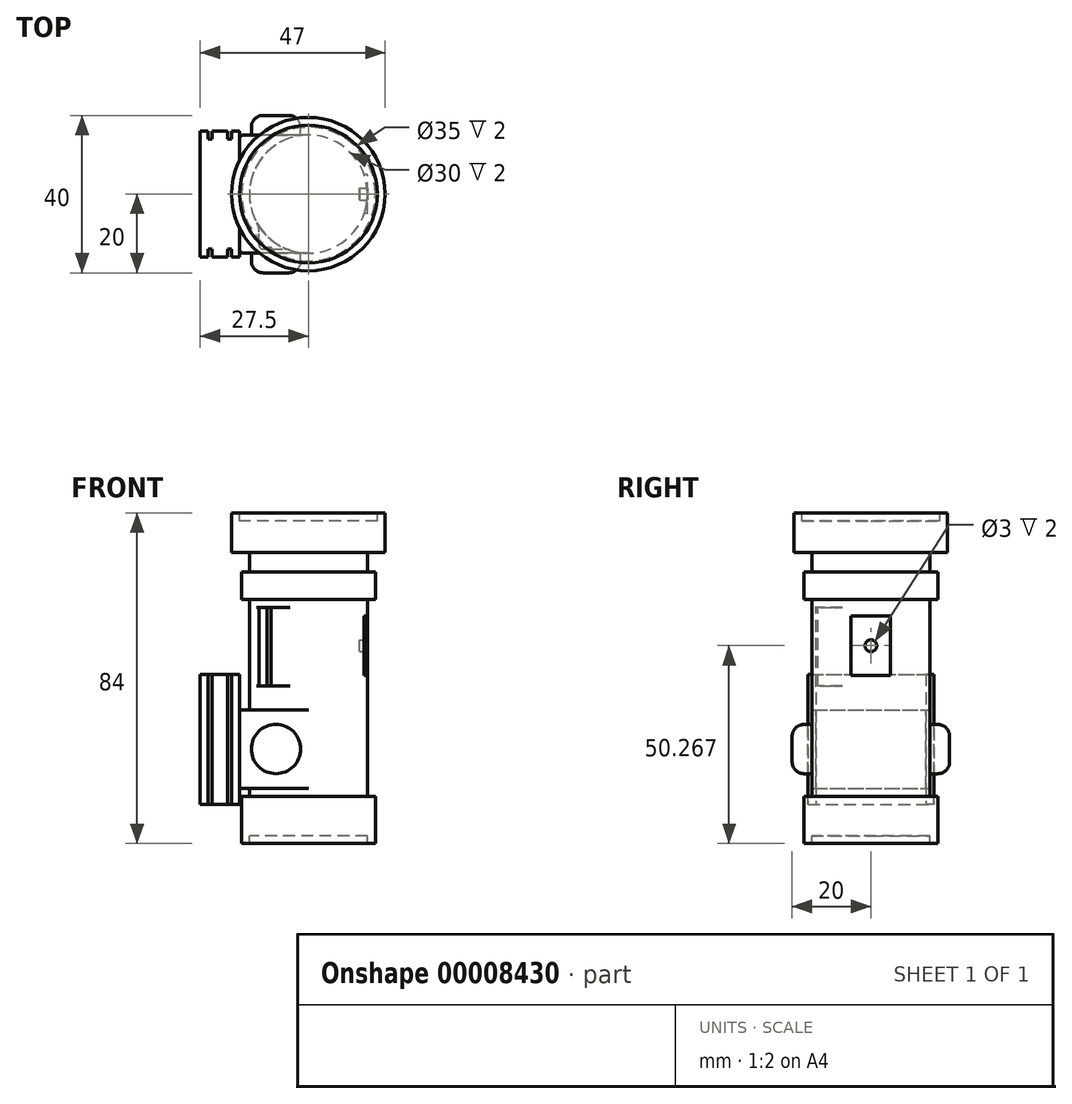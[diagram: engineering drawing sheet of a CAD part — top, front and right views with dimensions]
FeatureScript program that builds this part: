
annotation { "Feature Type Name" : "Feature", "Feature Type Description" : "" }
export const myFeature = defineFeature(function(context is Context, id is Id, definition is map)
    precondition{}
    {
        {
            var Q0;
            Q0=qCreatedBy(makeId("Front.planeOp"),FACE);
            var sketch = newSketch(context, id + "F0", { "sketchPlane" : qUnion([Q0])});
            skLineSegment(sketch, "E0", {"start": v(0, 0) * mm, "end": v(-15, 0) * mm});
            skLineSegment(sketch, "E1", {"start": v(-15, 0) * mm, "end": v(-15, -2) * mm});
            skLineSegment(sketch, "E2", {"start": v(-15, -2) * mm, "end": v(-17, -2) * mm});
            skLineSegment(sketch, "E3", {"start": v(-17, -2) * mm, "end": v(-17, 10) * mm});
            skLineSegment(sketch, "E4", {"start": v(-17, 10) * mm, "end": v(-15, 10) * mm});
            skLineSegment(sketch, "E5", {"start": v(-15, 10) * mm, "end": v(-15, 60) * mm});
            skLineSegment(sketch, "E6", {"start": v(-15, 60) * mm, "end": v(-17, 60) * mm});
            skLineSegment(sketch, "E7", {"start": v(-17, 60) * mm, "end": v(-17, 67) * mm});
            skLineSegment(sketch, "E8", {"start": v(-17, 67) * mm, "end": v(-15, 67) * mm});
            skLineSegment(sketch, "E9", {"start": v(-15, 67) * mm, "end": v(-15, 72) * mm});
            skLineSegment(sketch, "E10", {"start": v(-15, 72) * mm, "end": v(-19.5, 72) * mm});
            skLineSegment(sketch, "E11", {"start": v(-19.5, 72) * mm, "end": v(-19.5, 82) * mm});
            skLineSegment(sketch, "E12", {"start": v(-19.5, 82) * mm, "end": v(-17.5, 82) * mm});
            skLineSegment(sketch, "E13", {"start": v(-17.5, 82) * mm, "end": v(-17.5, 80) * mm});
            skLineSegment(sketch, "E14", {"start": v(-17.5, 80) * mm, "end": v(0, 80) * mm});
            skLineSegment(sketch, "E15", {"start": v(0, 80) * mm, "end": v(0, 0) * mm});
            skSolve(sketch);
        }
        {
            var Q0;
            Q0 = qSketchRegion(id + "F0", true);
            var Q1;
            Q1=sQuery(id+"F0.wireOp",EDGE,"E15");
            revolve(context, id + "F1", {"entities" : qUnion([Q0]), "axis" : qUnion([Q1]), "revolveType" : RevolveType.FULL});
        }
        {
            var Q0;
            Q0=qCreatedBy(makeId("Front.planeOp"),FACE);
            var sketch = newSketch(context, id + "F2", { "sketchPlane" : qUnion([Q0])});
            skLineSegment(sketch, "E16.bottom", {"start": v(15, 40.77) * mm, "end": v(12.59, 40.77) * mm});
            skLineSegment(sketch, "E16.top", {"start": v(15, 55.77) * mm, "end": v(12.59, 55.77) * mm});
            skLineSegment(sketch, "E16.left", {"start": v(15, 40.77) * mm, "end": v(15, 55.77) * mm});
            skLineSegment(sketch, "E16.right", {"start": v(12.59, 40.77) * mm, "end": v(12.59, 55.77) * mm});
            skSolve(sketch);
        }
        {
            var Q0;
            Q0 = qSketchRegion(id + "F2", true);
            extrude(context, id + "F3", {"entities" : qUnion([Q0]), "operationType" : NewBodyOperationType.ADD, "depth" : 5 * mm, "hasSecondDirection" : true, "secondDirectionOppositeDirection" : true, "secondDirectionDepth" : 5 * mm});
        }
        {
            var Q0;
            Q0=makeQuery(id+"F3.opExtrude","SWEPT_FACE",FACE,{"disambiguationData":[OSD([sQuery(id+"F2.wireOp",EDGE,"E16.left")])]});
            var sketch = newSketch(context, id + "F4", { "sketchPlane" : qUnion([Q0])});
            skCircle(sketch, "E17", {"center": v(0, 48.27) * mm, "radius": 1.5 * mm});
            skSolve(sketch);
        }
        {
            var Q0;
            Q0 = qSketchRegion(id + "F4", true);
            extrude(context, id + "F5", {"entities" : qUnion([Q0]), "operationType" : NewBodyOperationType.REMOVE, "oppositeDirection" : true, "depth" : 2 * mm});
        }
        {
            var Q0;
            Q0=qCreatedBy(makeId("Front.planeOp"),FACE);
            var sketch = newSketch(context, id + "F6", { "sketchPlane" : qUnion([Q0])});
            skLineSegment(sketch, "E18.bottom", {"start": v(-12.5, 38) * mm, "end": v(-2.5, 38) * mm});
            skLineSegment(sketch, "E18.top", {"start": v(-12.5, 58) * mm, "end": v(-2.5, 58) * mm});
            skLineSegment(sketch, "E18.left", {"start": v(-12.5, 38) * mm, "end": v(-12.5, 58) * mm});
            skLineSegment(sketch, "E18.right", {"start": v(-2.5, 38) * mm, "end": v(-2.5, 58) * mm});
            skSolve(sketch);
        }
        {
            var Q0;
            Q0 = qSketchRegion(id + "F6", true);
            extrude(context, id + "F7", {"entities" : qUnion([Q0]), "operationType" : NewBodyOperationType.ADD, "depth" : 14 * mm});
        }
        {
            var Q0;
            Q0=makeQuery(id+"F7.boolean.opBoolean","INTERSECT",EDGE,{"derivedFrom":[makeQuery(id+"F1.opRevolve","SWEPT_FACE",FACE,{"disambiguationData":[OSD([sQuery(id+"F0.wireOp",EDGE,"E5")])]}),makeQuery(id+"F7.opExtrude","CAP_FACE",FACE,{"disambiguationData":[OSD([sQuery(id+"F6.wireOp",EDGE,"E18.bottom"),sQuery(id+"F6.wireOp",EDGE,"E18.top"),sQuery(id+"F6.wireOp",EDGE,"E18.left"),sQuery(id+"F6.wireOp",EDGE,"E18.right")])],"isStart":false})]});
            var Q1;
            Q1=makeQuery(id+"F7.boolean.opBoolean","INTERSECT",EDGE,{"derivedFrom":[makeQuery(id+"F1.opRevolve","SWEPT_FACE",FACE,{"disambiguationData":[OSD([sQuery(id+"F0.wireOp",EDGE,"E5")])]}),makeQuery(id+"F7.opExtrude","SWEPT_FACE",FACE,{"disambiguationData":[OSD([sQuery(id+"F6.wireOp",EDGE,"E18.left")])]})]});
            fillet(context, id + "F8", {"entities" : qUnion([Q0, Q1]), "radius" : 5 * mm, "tangentPropagation" : true, "allowEdgeOverflow" : false});
        }
        {
            var Q0;
            Q0=makeQuery(id+"F7.opExtrude","CAP_EDGE",EDGE,{"disambiguationData":[OSD([sQuery(id+"F6.wireOp",EDGE,"E18.left")])],"isStart":false});
            fillet(context, id + "F9", {"entities" : qUnion([Q0]), "radius" : 1 * mm, "tangentPropagation" : true, "allowEdgeOverflow" : false});
        }
        {
            var Q0;
            Q0=makeQuery(id+"F7.opExtrude","CAP_FACE",FACE,{"disambiguationData":[OSD([sQuery(id+"F6.wireOp",EDGE,"E18.bottom"),sQuery(id+"F6.wireOp",EDGE,"E18.top"),sQuery(id+"F6.wireOp",EDGE,"E18.left"),sQuery(id+"F6.wireOp",EDGE,"E18.right")])],"isStart":false});
            var sketch = newSketch(context, id + "F10", { "sketchPlane" : qUnion([Q0])});
            skLineSegment(sketch, "E19.bottom", {"start": v(-10.5, 38) * mm, "end": v(-9.5, 38) * mm});
            skLineSegment(sketch, "E19.top", {"start": v(-10.5, 58) * mm, "end": v(-9.5, 58) * mm});
            skLineSegment(sketch, "E19.left", {"start": v(-10.5, 38) * mm, "end": v(-10.5, 58) * mm});
            skLineSegment(sketch, "E19.right", {"start": v(-9.5, 38) * mm, "end": v(-9.5, 58) * mm});
            skSolve(sketch);
        }
        {
            var Q0;
            Q0 = qSketchRegion(id + "F10", true);
            extrude(context, id + "F11", {"entities" : qUnion([Q0]), "operationType" : NewBodyOperationType.REMOVE, "oppositeDirection" : true, "depth" : 0.5 * mm});
        }
        {
            var Q0;
            Q0=qCreatedBy(makeId("Front.planeOp"),FACE);
            var sketch = newSketch(context, id + "F12", { "sketchPlane" : qUnion([Q0])});
            skLineSegment(sketch, "E20.bottom", {"start": v(0, 12) * mm, "end": v(-17.5, 12) * mm});
            skLineSegment(sketch, "E20.top", {"start": v(0, 32) * mm, "end": v(-17.5, 32) * mm});
            skLineSegment(sketch, "E20.left", {"start": v(0, 12) * mm, "end": v(0, 32) * mm});
            skLineSegment(sketch, "E20.right", {"start": v(-17.5, 12) * mm, "end": v(-17.5, 32) * mm});
            skSolve(sketch);
        }
        {
            var Q0;
            Q0 = qSketchRegion(id + "F12", true);
            extrude(context, id + "F13", {"entities" : qUnion([Q0]), "operationType" : NewBodyOperationType.ADD, "depth" : 15 * mm, "hasSecondDirection" : true, "secondDirectionOppositeDirection" : true, "secondDirectionDepth" : 15 * mm});
        }
        {
            var Q0;
            Q0=makeQuery(id+"F13.opExtrude","CAP_EDGE",EDGE,{"disambiguationData":[OSD([sQuery(id+"F12.wireOp",EDGE,"E20.right")])],"isStart":true});
            var Q1;
            Q1=makeQuery(id+"F13.opExtrude","CAP_EDGE",EDGE,{"disambiguationData":[OSD([sQuery(id+"F12.wireOp",EDGE,"E20.right")])],"isStart":false});
            var Q2;
            Q2=makeQuery(id+"F13.opExtrude","CAP_EDGE",EDGE,{"disambiguationData":[OSD([sQuery(id+"F12.wireOp",EDGE,"E20.left")])],"isStart":true});
            var Q3;
            Q3=makeQuery(id+"F13.opExtrude","CAP_EDGE",EDGE,{"disambiguationData":[OSD([sQuery(id+"F12.wireOp",EDGE,"E20.left")])],"isStart":false});
            fillet(context, id + "F14", {"entities" : qUnion([Q0, Q1, Q2, Q3]), "radius" : 1 * mm, "tangentPropagation" : true, "allowEdgeOverflow" : false});
        }
        {
            var Q0;
            Q0=makeQuery(id+"F13.opExtrude","CAP_FACE",FACE,{"disambiguationData":[OSD([sQuery(id+"F12.wireOp",EDGE,"E20.bottom"),sQuery(id+"F12.wireOp",EDGE,"E20.top"),sQuery(id+"F12.wireOp",EDGE,"E20.left"),sQuery(id+"F12.wireOp",EDGE,"E20.right")])],"isStart":false});
            var sketch = newSketch(context, id + "F15", { "sketchPlane" : qUnion([Q0])});
            skCircle(sketch, "E21", {"center": v(-8.25, 22) * mm, "radius": 6.25 * mm});
            skSolve(sketch);
        }
        {
            var Q0;
            Q0 = qSketchRegion(id + "F15", true);
            extrude(context, id + "F16", {"entities" : qUnion([Q0]), "operationType" : NewBodyOperationType.ADD, "depth" : 5 * mm, "hasSecondDirection" : true, "secondDirectionOppositeDirection" : true, "secondDirectionDepth" : 35 * mm});
        }
        {
            var Q0;
            Q0=makeQuery(id+"F16.opExtrude","CAP_EDGE",EDGE,{"disambiguationData":[OSD([sQuery(id+"F15.wireOp",EDGE,"E21")])],"isStart":false});
            var Q1;
            Q1=makeQuery(id+"F16.opExtrude","CAP_EDGE",EDGE,{"disambiguationData":[OSD([sQuery(id+"F15.wireOp",EDGE,"E21")])],"isStart":true});
            fillet(context, id + "F17", {"entities" : qUnion([Q0, Q1]), "radius" : 3 * mm, "tangentPropagation" : true, "allowEdgeOverflow" : false});
        }
        {
            var Q0;
            Q0=makeQuery(id+"F13.opExtrude","SWEPT_FACE",FACE,{"disambiguationData":[OSD([sQuery(id+"F12.wireOp",EDGE,"E20.right")])]});
            var sketch = newSketch(context, id + "F18", { "sketchPlane" : qUnion([Q0])});
            skLineSegment(sketch, "E22.bottom", {"start": v(16, 8) * mm, "end": v(-16, 8) * mm});
            skLineSegment(sketch, "E22.top", {"start": v(16, 41) * mm, "end": v(-16, 41) * mm});
            skLineSegment(sketch, "E22.left", {"start": v(16, 8) * mm, "end": v(16, 41) * mm});
            skLineSegment(sketch, "E22.right", {"start": v(-16, 8) * mm, "end": v(-16, 41) * mm});
            skSolve(sketch);
        }
        {
            var Q0;
            Q0 = qSketchRegion(id + "F18", true);
            extrude(context, id + "F19", {"entities" : qUnion([Q0]), "operationType" : NewBodyOperationType.ADD, "depth" : 10 * mm});
        }
        {
            var Q0;
            Q0=makeQuery(id+"F19.opExtrude","SWEPT_FACE",FACE,{"disambiguationData":[OSD([sQuery(id+"F18.wireOp",EDGE,"E22.bottom")])]});
            var sketch = newSketch(context, id + "F20", { "sketchPlane" : qUnion([Q0])});
            skLineSegment(sketch, "E23.bottom", {"start": v(-25.5, 16) * mm, "end": v(-24.5, 16) * mm});
            skLineSegment(sketch, "E23.top", {"start": v(-25.5, 14) * mm, "end": v(-24.5, 14) * mm});
            skLineSegment(sketch, "E23.left", {"start": v(-25.5, 16) * mm, "end": v(-25.5, 14) * mm});
            skLineSegment(sketch, "E23.right", {"start": v(-24.5, 16) * mm, "end": v(-24.5, 14) * mm});
            skLineSegment(sketch, "E24.bottom", {"start": v(-20.5, 16) * mm, "end": v(-19.5, 16) * mm});
            skLineSegment(sketch, "E24.top", {"start": v(-20.5, 14) * mm, "end": v(-19.5, 14) * mm});
            skLineSegment(sketch, "E24.left", {"start": v(-20.5, 16) * mm, "end": v(-20.5, 14) * mm});
            skLineSegment(sketch, "E24.right", {"start": v(-19.5, 16) * mm, "end": v(-19.5, 14) * mm});
            skLineSegment(sketch, "E25.bottom", {"start": v(-25.5, -16) * mm, "end": v(-24.5, -16) * mm});
            skLineSegment(sketch, "E25.top", {"start": v(-25.5, -14) * mm, "end": v(-24.5, -14) * mm});
            skLineSegment(sketch, "E25.left", {"start": v(-25.5, -16) * mm, "end": v(-25.5, -14) * mm});
            skLineSegment(sketch, "E25.right", {"start": v(-24.5, -16) * mm, "end": v(-24.5, -14) * mm});
            skLineSegment(sketch, "E26.bottom", {"start": v(-20.5, -16) * mm, "end": v(-19.5, -16) * mm});
            skLineSegment(sketch, "E26.top", {"start": v(-20.5, -14) * mm, "end": v(-19.5, -14) * mm});
            skLineSegment(sketch, "E26.left", {"start": v(-20.5, -16) * mm, "end": v(-20.5, -14) * mm});
            skLineSegment(sketch, "E26.right", {"start": v(-19.5, -16) * mm, "end": v(-19.5, -14) * mm});
            skSolve(sketch);
        }
        {
            var Q0;
            Q0 = qSketchRegion(id + "F20", true);
            extrude(context, id + "F21", {"entities" : qUnion([Q0]), "operationType" : NewBodyOperationType.REMOVE, "oppositeDirection" : true, "depth" : 35 * mm});
        }
    });
